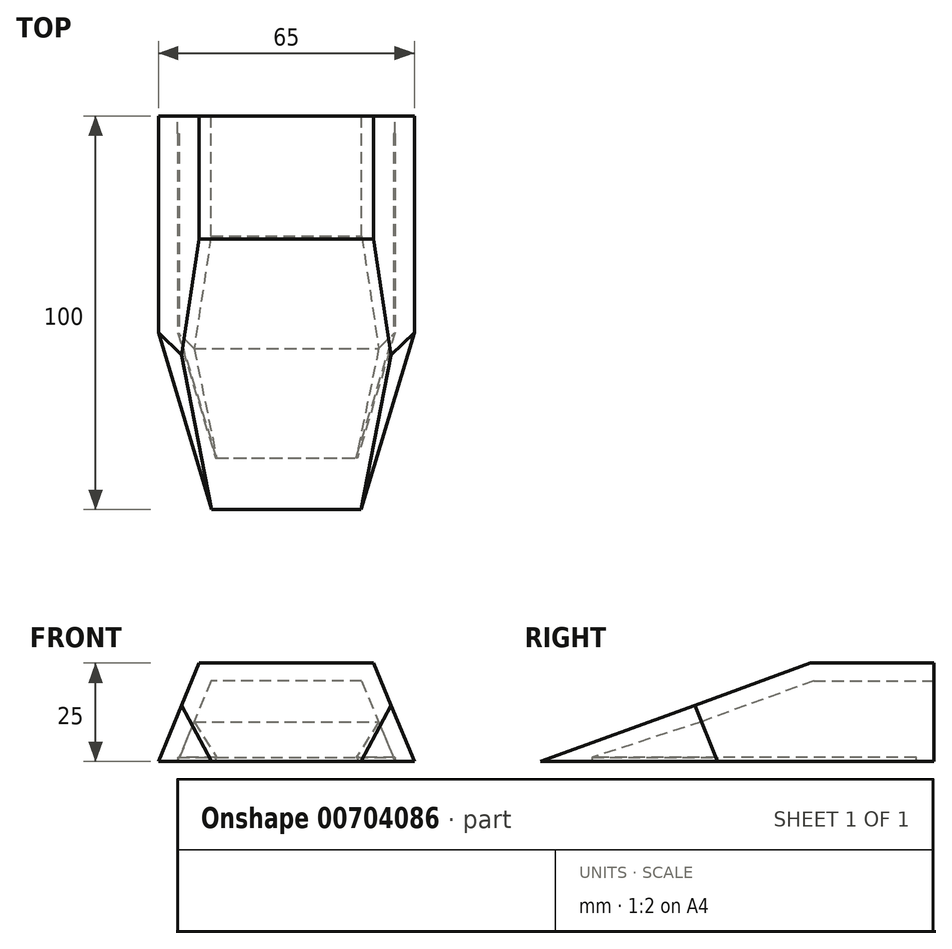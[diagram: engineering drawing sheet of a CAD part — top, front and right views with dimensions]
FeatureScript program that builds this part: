
annotation { "Feature Type Name" : "Feature", "Feature Type Description" : "" }
export const myFeature = defineFeature(function(context is Context, id is Id, definition is map)
    precondition{}
    {
        {
            var Q0;
            Q0=qCreatedBy(makeId("Top.planeOp"),FACE);
            var sketch = newSketch(context, id + "F0", { "sketchPlane" : qUnion([Q0])});
            skLineSegment(sketch, "E0.bottom", {"start": v(0, 55) * mm, "end": v(32.5, 55) * mm});
            skLineSegment(sketch, "E0.left", {"start": v(0, 55) * mm, "end": v(0, 0) * mm});
            skLineSegment(sketch, "E0.right", {"start": v(32.5, 55) * mm, "end": v(32.5, -45) * mm});
            skLineSegment(sketch, "E1", {"start": v(0, 0) * mm, "end": v(13.54, -45) * mm});
            skLineSegment(sketch, "E2", {"start": v(13.54, -45) * mm, "end": v(32.5, -45) * mm});
            skSolve(sketch);
        }
        {
            var Q0;
            Q0=qSketchRegion(id+"F0",true);
            extrude(context, id + "F1", {"entities" : qUnion([Q0]), "depth" : 25 * mm});
        }
        {
            var Q0;
            Q0=qCreatedBy(makeId("Right.planeOp"),FACE);
            cPlane(context, id + "F2", {"entities" : qUnion([Q0]), "cplaneType" : CPlaneType.OFFSET, "offset" : 32.5 * mm, "width" : 150 * mm, "height" : 150 * mm});
        }
        {
            var Q0;
            Q0=makeQuery(id+"F1.opExtrude","SWEPT_FACE",FACE,{"disambiguationData":[OSD([sQuery(id+"F0.wireOp",EDGE,"E0.bottom")])]});
            var sketch = newSketch(context, id + "F3", { "sketchPlane" : qUnion([Q0])});
            skLineSegment(sketch, "E3", {"start": v(0, 0) * mm, "end": v(-10.36, 25) * mm});
            skLineSegment(sketch, "E4", {"start": v(-10.36, 25) * mm, "end": v(0, 25) * mm});
            skLineSegment(sketch, "E5", {"start": v(0, 25) * mm, "end": v(0, 0) * mm});
            skSolve(sketch);
        }
        {
            var Q0;
            Q0=qSketchRegion(id+"F3",true);
            extrude(context, id + "F4", {"entities" : qUnion([Q0]), "operationType" : NewBodyOperationType.REMOVE, "endBound" : BoundingType.THROUGH_ALL, "oppositeDirection" : true, "depth" : 25 * mm});
        }
        {
            var Q0;
            Q0=makeQuery(id+"F1.opExtrude","SWEPT_FACE",FACE,{"disambiguationData":[OSD([sQuery(id+"F0.wireOp",EDGE,"E2")])]});
            var sketch = newSketch(context, id + "F5", { "sketchPlane" : qUnion([Q0])});
            skLineSegment(sketch, "E6", {"start": v(13.54, 0) * mm, "end": v(20.86, 25) * mm});
            skLineSegment(sketch, "E7", {"start": v(20.86, 25) * mm, "end": v(13.54, 25) * mm});
            skLineSegment(sketch, "E8", {"start": v(13.54, 25) * mm, "end": v(13.54, 0) * mm});
            skSolve(sketch);
        }
        {
            var Q0;
            Q0=makeQuery(id+"F1.opExtrude","CAP_FACE",FACE,{"disambiguationData":[OSD([sQuery(id+"F0.wireOp",EDGE,"E0.bottom"),sQuery(id+"F0.wireOp",EDGE,"E0.left"),sQuery(id+"F0.wireOp",EDGE,"E0.right"),sQuery(id+"F0.wireOp",EDGE,"E1"),sQuery(id+"F0.wireOp",EDGE,"E2")])],"isStart":true});
            var sketch = newSketch(context, id + "F6", { "sketchPlane" : qUnion([Q0])});
            skLineSegment(sketch, "E9", {"start": v(13.54, 45) * mm, "end": v(-8.73, -29) * mm});
            skSolve(sketch);
        }
        {
            var Q0;
            Q0=makeQuery(id+"F5.imprint","IMPRINT",FACE,{"disambiguationData":[TD([[makeQuery(id+"F5.imprint","IMPRINT",EDGE,{"derivedFrom":sQuery(id+"F5.wireOp",EDGE,"E6")}),1.0]])]});
            var Q1;
            Q1=sQuery(id+"F6.wireOp",EDGE,"E9");
            sweep(context, id + "F7", {"operationType" : NewBodyOperationType.REMOVE, "profiles" : qUnion([Q0]), "path" : qUnion([Q1])});
        }
        {
            var Q0;
            Q0=makeQuery(id+"F1.opExtrude","SWEPT_FACE",FACE,{"disambiguationData":[OSD([sQuery(id+"F0.wireOp",EDGE,"E0.right")])]});
            var sketch = newSketch(context, id + "F8", { "sketchPlane" : qUnion([Q0])});
            skLineSegment(sketch, "E10", {"start": v(-45, 0) * mm, "end": v(23.69, 25) * mm});
            skLineSegment(sketch, "E11", {"start": v(23.69, 25) * mm, "end": v(-45, 25) * mm});
            skLineSegment(sketch, "E12", {"start": v(-45, 25) * mm, "end": v(-45, 0) * mm});
            skSolve(sketch);
        }
        {
            var Q0;
            Q0=qSketchRegion(id+"F8",true);
            extrude(context, id + "F9", {"entities" : qUnion([Q0]), "operationType" : NewBodyOperationType.REMOVE, "endBound" : BoundingType.THROUGH_ALL, "oppositeDirection" : true, "depth" : 25 * mm});
        }
        {
            var Q0;
            Q0=makeQuery(id+"F1.opExtrude","CAP_FACE",FACE,{"disambiguationData":[OSD([sQuery(id+"F0.wireOp",EDGE,"E0.bottom"),sQuery(id+"F0.wireOp",EDGE,"E0.left"),sQuery(id+"F0.wireOp",EDGE,"E0.right"),sQuery(id+"F0.wireOp",EDGE,"E1"),sQuery(id+"F0.wireOp",EDGE,"E2")])],"isStart":true});
            var Q1;
            Q1=makeQuery(id+"F1.opExtrude","SWEPT_FACE",FACE,{"disambiguationData":[OSD([sQuery(id+"F0.wireOp",EDGE,"E0.right")])]});
            shell(context, id + "F10", {"entities" : qUnion([Q0, Q1]), "thickness" : 4.5 * mm});
        }
        {
            var Q0;
            Q0=makeQuery(id+"F1.opExtrude","CAP_FACE",FACE,{"disambiguationData":[OSD([sQuery(id+"F0.wireOp",EDGE,"E0.bottom"),sQuery(id+"F0.wireOp",EDGE,"E0.left"),sQuery(id+"F0.wireOp",EDGE,"E0.right"),sQuery(id+"F0.wireOp",EDGE,"E1"),sQuery(id+"F0.wireOp",EDGE,"E2")])],"isStart":true});
            var sketch = newSketch(context, id + "F11", { "sketchPlane" : qUnion([Q0])});
            skLineSegment(sketch, "E13", {"start": v(32.5, 31.84) * mm, "end": v(14.46, 31.84) * mm});
            skLineSegment(sketch, "E14", {"start": v(14.46, 31.84) * mm, "end": v(4.87, -0.03) * mm});
            skLineSegment(sketch, "E15", {"start": v(4.87, -0.03) * mm, "end": v(4.87, -50.5) * mm});
            skLineSegment(sketch, "E16", {"start": v(4.87, -50.5) * mm, "end": v(32.5, -50.5) * mm});
            skLineSegment(sketch, "E17", {"start": v(32.5, -50.5) * mm, "end": v(32.5, 31.84) * mm});
            skSolve(sketch);
        }
        {
            var Q0;
            Q0=qSketchRegion(id+"F11",true);
            extrude(context, id + "F12", {"entities" : qUnion([Q0]), "operationType" : NewBodyOperationType.REMOVE, "oppositeDirection" : true, "depth" : 1 * mm, "offsetDistance" : 25 * mm});
        }
        {
            var Q0;
            Q0=makeQuery(id+"F1.opExtrude","SWEPT_FACE",FACE,{"disambiguationData":[OSD([sQuery(id+"F0.wireOp",EDGE,"E0.bottom")])]});
            var sketch = newSketch(context, id + "F13", { "sketchPlane" : qUnion([Q0])});
            skLineSegment(sketch, "E18", {"start": v(-32.5, 20.5) * mm, "end": v(-13.36, 20.5) * mm});
            skLineSegment(sketch, "E19", {"start": v(-13.36, 20.5) * mm, "end": v(-4.87, 0) * mm});
            skLineSegment(sketch, "E20", {"start": v(-4.87, 0) * mm, "end": v(-32.5, 0) * mm});
            skLineSegment(sketch, "E21", {"start": v(-32.5, 0) * mm, "end": v(-32.5, 20.5) * mm});
            skSolve(sketch);
        }
        {
            var Q0;
            Q0=qSketchRegion(id+"F13",true);
            var Q1;
            Q1=makeQuery(id+"F12.boolean.opBoolean","MERGE",FACE,{"derivedFrom":[makeQuery(id+"F10.opShell","OFFSET_FACE",FACE,{"disambiguationData":[OSD([sQuery(id+"F0.wireOp",EDGE,"E0.bottom")])]}),makeQuery(id+"F12.opExtrude","SWEPT_FACE",FACE,{"disambiguationData":[OSD([sQuery(id+"F11.wireOp",EDGE,"E16")])]})]});
            extrude(context, id + "F14", {"entities" : qUnion([Q0]), "operationType" : NewBodyOperationType.REMOVE, "endBound" : BoundingType.UP_TO_SURFACE, "oppositeDirection" : true, "depth" : 25 * mm, "endBoundEntityFace" : qUnion([Q1]), "offsetDistance" : 25 * mm});
        }
        {
            var Q0;
            Q0=makeQuery(id+"F1.opExtrude","SWEPT_FACE",FACE,{"disambiguationData":[OSD([sQuery(id+"F0.wireOp",EDGE,"E0.right")])]});
            var sketch = newSketch(context, id + "F15", { "sketchPlane" : qUnion([Q0])});
            skLineSegment(sketch, "E22", {"start": v(-31.84, 1) * mm, "end": v(-4.05, 10.11) * mm});
            skLineSegment(sketch, "E23", {"start": v(-4.05, 10.11) * mm, "end": v(-29.1, 1) * mm});
            skLineSegment(sketch, "E24", {"start": v(-29.1, 1) * mm, "end": v(-31.84, 1) * mm});
            skSolve(sketch);
        }
        {
            var Q0;
            Q0=qSketchRegion(id+"F15",true);
            var Q1;
            Q1=makeQuery(id+"F10.opShell","OFFSET_FACE",FACE,{"disambiguationData":[OSD([sQuery(id+"F5.wireOp",EDGE,"E6"),sQuery(id+"F6.wireOp",EDGE,"E9")])]});
            extrude(context, id + "F16", {"entities" : qUnion([Q0]), "operationType" : NewBodyOperationType.REMOVE, "endBound" : BoundingType.UP_TO_SURFACE, "oppositeDirection" : true, "depth" : 25 * mm, "endBoundEntityFace" : qUnion([Q1]), "offsetDistance" : 25 * mm});
        }
        {
            var Q0;
            Q0=makeQuery(id+"F1.opExtrude","SWEPT_BODY",BODY,{"disambiguationData":[OSD([sQuery(id+"F0.wireOp",EDGE,"E0.bottom"),sQuery(id+"F0.wireOp",EDGE,"E0.left"),sQuery(id+"F0.wireOp",EDGE,"E0.right"),sQuery(id+"F0.wireOp",EDGE,"E1"),sQuery(id+"F0.wireOp",EDGE,"E2")])]});
            var Q1;
            Q1=qCreatedBy(id+"F2.planeOp",FACE);
            mirror(context, id + "F17", {"operationType" : NewBodyOperationType.ADD, "entities" : qUnion([Q0]), "mirrorPlane" : qUnion([Q1])});
        }
    });
